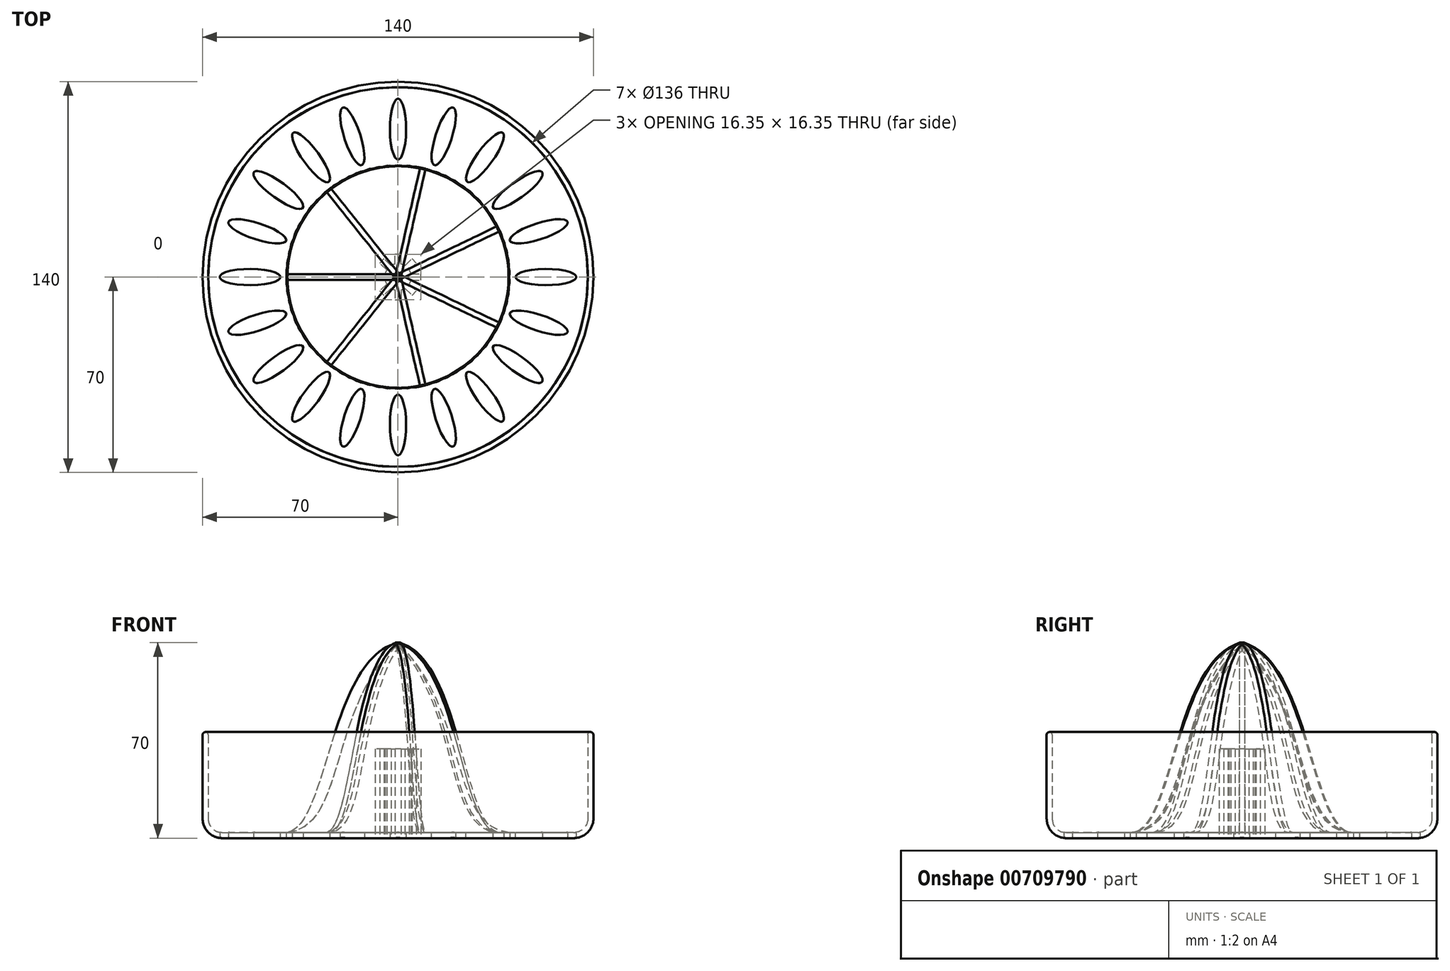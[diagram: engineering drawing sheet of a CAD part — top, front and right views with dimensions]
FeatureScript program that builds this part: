
annotation { "Feature Type Name" : "Feature", "Feature Type Description" : "" }
export const myFeature = defineFeature(function(context is Context, id is Id, definition is map)
    precondition{}
    {
        {
            var Q0;
            Q0=qCreatedBy(makeId("Front.planeOp"),FACE);
            var sketch = newSketch(context, id + "F0", { "sketchPlane" : qUnion([Q0])});
            skFitSpline(sketch, "E0", {"points": [v(0, 68) * mm, v(-40, 0) * mm], "startDerivative": vector(-73.69, -17.1) * mm, "endDerivative": vector(-44.25, -4.31) * mm});
            skLineSegment(sketch, "E1", {"start": v(-63, -2) * mm, "end": v(0, -2) * mm});
            skLineSegment(sketch, "E2", {"start": v(0, -2) * mm, "end": v(0, 68) * mm});
            skLineSegment(sketch, "E3", {"start": v(-70, 5) * mm, "end": v(-70, 35) * mm});
            skLineSegment(sketch, "E4", {"start": v(-69, 36) * mm, "end": v(-69, 36) * mm});
            skLineSegment(sketch, "E5", {"start": v(-68, 35) * mm, "end": v(-68, 5) * mm});
            skLineSegment(sketch, "E6", {"start": v(-63, 0) * mm, "end": v(-40, 0) * mm});
            skPoint(sketch, "E7.visualSharp", {"position": v(-68, 0) * mm});
            skArc(sketch, "E7.filletArc", {"start": v(-68, 5) * mm, "mid": v(-66.54, 1.46) * mm, "end": v(-63, 0) * mm});
            skPoint(sketch, "E8.visualSharp", {"position": v(-70, -2) * mm});
            skArc(sketch, "E8.filletArc", {"start": v(-70, 5) * mm, "mid": v(-67.95, 0.05) * mm, "end": v(-63, -2) * mm});
            skPoint(sketch, "E9.visualSharp", {"position": v(-70, 36) * mm});
            skArc(sketch, "E9.filletArc", {"start": v(-69, 36) * mm, "mid": v(-69.7, 35.7) * mm, "end": v(-70, 35) * mm});
            skPoint(sketch, "E10.visualSharp", {"position": v(-68, 36) * mm});
            skArc(sketch, "E10.filletArc", {"start": v(-68, 35) * mm, "mid": v(-68.3, 35.7) * mm, "end": v(-69, 36) * mm});
            skFitSpline(sketch, "E11", {"points": [v(0, 68) * mm, v(-40, 0) * mm], "startDerivative": vector(-76.4, -73) * mm, "endDerivative": vector(-64.41, -4.31) * mm});
            skLineSegment(sketch, "E12", {"start": v(-40, 0) * mm, "end": v(0, 0) * mm});
            skSolve(sketch);
        }
        {
            var Q0;
            Q0=makeQuery(id+"F0.imprint","IMPRINT",FACE,{"disambiguationData":[TD([[makeQuery(id+"F0.imprint","IMPRINT",EDGE,{"derivedFrom":sQuery(id+"F0.wireOp",EDGE,"E1")}),1.0]])]});
            var Q1;
            {var subQ0=sQuery(id+"F0.wireOp",EDGE,"E11");Q1=makeQuery(id+"F0.imprint","IMPRINT",FACE,{"disambiguationData":[TD([[makeQuery(id+"F0.imprint","IMPRINT",EDGE,{"derivedFrom":subQ0}),1.0]])]});}
            var Q2;
            Q2=sQuery(id+"F0.wireOp",EDGE,"E2");
            revolve(context, id + "F1", {"surfaceOperationType" : NewSurfaceOperationType.NEW, "entities" : qUnion([Q0, Q1]), "axis" : qUnion([Q2]), "revolveType" : RevolveType.FULL});
        }
        {
            var Q0;
            Q0=qCreatedBy(makeId("Top.planeOp"),FACE);
            var sketch = newSketch(context, id + "F2", { "sketchPlane" : qUnion([Q0])});
            skEllipse(sketch, "E13", {"center": v(-52.98, 0) * mm, "majorRadius": 10.85 * mm, "minorRadius": 2.91 * mm, "majorAxis": v(1, 0)});
            skEllipse(sketch, "E14.1.0", {"center": v(-50.4, -16.37) * mm, "majorRadius": 10.85 * mm, "minorRadius": 2.91 * mm, "majorAxis": v(0.95, 0.3)});
            skEllipse(sketch, "E14.2.0", {"center": v(-42.87, -31.14) * mm, "majorRadius": 10.85 * mm, "minorRadius": 2.91 * mm, "majorAxis": v(0.8, 0.59)});
            skEllipse(sketch, "E14.3.0", {"center": v(-31.14, -42.87) * mm, "majorRadius": 10.85 * mm, "minorRadius": 2.91 * mm, "majorAxis": v(0.59, 0.8)});
            skEllipse(sketch, "E14.4.0", {"center": v(-16.37, -50.4) * mm, "majorRadius": 10.85 * mm, "minorRadius": 2.91 * mm, "majorAxis": v(0.3, 0.95)});
            skEllipse(sketch, "E14.5.0", {"center": v(0, -52.98) * mm, "majorRadius": 10.85 * mm, "minorRadius": 2.91 * mm, "majorAxis": v(0, 1)});
            skEllipse(sketch, "E14.6.0", {"center": v(16.37, -50.4) * mm, "majorRadius": 10.85 * mm, "minorRadius": 2.91 * mm, "majorAxis": v(-0.3, 0.95)});
            skEllipse(sketch, "E14.7.0", {"center": v(31.14, -42.87) * mm, "majorRadius": 10.85 * mm, "minorRadius": 2.91 * mm, "majorAxis": v(-0.59, 0.8)});
            skEllipse(sketch, "E14.8.0", {"center": v(42.87, -31.14) * mm, "majorRadius": 10.85 * mm, "minorRadius": 2.91 * mm, "majorAxis": v(-0.8, 0.59)});
            skEllipse(sketch, "E14.9.0", {"center": v(50.4, -16.37) * mm, "majorRadius": 10.85 * mm, "minorRadius": 2.91 * mm, "majorAxis": v(-0.95, 0.3)});
            skEllipse(sketch, "E14.10.0", {"center": v(52.98, 0) * mm, "majorRadius": 10.85 * mm, "minorRadius": 2.91 * mm, "majorAxis": v(-1, 0)});
            skEllipse(sketch, "E14.11.0", {"center": v(50.4, 16.37) * mm, "majorRadius": 10.85 * mm, "minorRadius": 2.91 * mm, "majorAxis": v(-0.95, -0.3)});
            skEllipse(sketch, "E14.12.0", {"center": v(42.87, 31.14) * mm, "majorRadius": 10.85 * mm, "minorRadius": 2.91 * mm, "majorAxis": v(-0.8, -0.59)});
            skEllipse(sketch, "E14.13.0", {"center": v(31.14, 42.87) * mm, "majorRadius": 10.85 * mm, "minorRadius": 2.91 * mm, "majorAxis": v(-0.59, -0.8)});
            skEllipse(sketch, "E14.14.0", {"center": v(16.37, 50.4) * mm, "majorRadius": 10.85 * mm, "minorRadius": 2.91 * mm, "majorAxis": v(-0.3, -0.95)});
            skEllipse(sketch, "E14.15.0", {"center": v(0, 52.98) * mm, "majorRadius": 10.85 * mm, "minorRadius": 2.91 * mm, "majorAxis": v(0, -1)});
            skEllipse(sketch, "E14.16.0", {"center": v(-16.37, 50.4) * mm, "majorRadius": 10.85 * mm, "minorRadius": 2.91 * mm, "majorAxis": v(0.3, -0.95)});
            skEllipse(sketch, "E14.17.0", {"center": v(-31.14, 42.87) * mm, "majorRadius": 10.85 * mm, "minorRadius": 2.91 * mm, "majorAxis": v(0.59, -0.8)});
            skEllipse(sketch, "E14.18.0", {"center": v(-42.87, 31.14) * mm, "majorRadius": 10.85 * mm, "minorRadius": 2.91 * mm, "majorAxis": v(0.8, -0.59)});
            skEllipse(sketch, "E14.19.0", {"center": v(-50.4, 16.37) * mm, "majorRadius": 10.85 * mm, "minorRadius": 2.91 * mm, "majorAxis": v(0.95, -0.3)});
            skPoint(sketch, "E14.center", {"position": v(0, 0) * mm});
            skSolve(sketch);
        }
        {
            var Q0;
            {var subQ0=sQuery(id+"F0.wireOp",EDGE,"E11");Q0=makeQuery(id+"F0.imprint","IMPRINT",FACE,{"disambiguationData":[TD([[makeQuery(id+"F0.imprint","IMPRINT",EDGE,{"derivedFrom":subQ0}),1.0]])]});}
            var Q1;
            Q1=makeQuery(id+"F0.imprint","IMPRINT",FACE,{"disambiguationData":[TD([[makeQuery(id+"F0.imprint","IMPRINT",EDGE,{"derivedFrom":sQuery(id+"F0.wireOp",EDGE,"E0")}),1.0]])]});
            extrude(context, id + "F3", {"entities" : qUnion([Q0, Q1]), "operationType" : NewBodyOperationType.ADD, "endBound" : BoundingType.SYMMETRIC, "depth" : 2 * mm, "offsetDistance" : 25 * mm});
        }
        {
            var Q0;
            Q0=makeQuery(id+"F1.opRevolve","SWEPT_BODY",BODY,{"disambiguationData":[OSD([sQuery(id+"F0.wireOp",EDGE,"E1"),sQuery(id+"F0.wireOp",EDGE,"E2"),sQuery(id+"F0.wireOp",EDGE,"E3"),sQuery(id+"F0.wireOp",EDGE,"E5"),sQuery(id+"F0.wireOp",EDGE,"E6"),sQuery(id+"F0.wireOp",EDGE,"E7.filletArc"),sQuery(id+"F0.wireOp",EDGE,"E8.filletArc"),sQuery(id+"F0.wireOp",EDGE,"E9.filletArc"),sQuery(id+"F0.wireOp",EDGE,"E10.filletArc"),sQuery(id+"F0.wireOp",EDGE,"E11")])]});
            var Q1;
            Q1=sQuery(id+"F0.wireOp",EDGE,"E2");
            circularPattern(context, id + "F4", {"entities" : qUnion([Q0]), "axis" : qUnion([Q1]), "angle" : 360 * degree, "instanceCount" : 7, "equalSpace" : true});
        }
        {
            var Q0;
            Q0=makeQuery(id+"F1.opRevolve","SWEPT_FACE",FACE,{"disambiguationData":[OSD([sQuery(id+"F0.wireOp",EDGE,"E1")])]});
            var sketch = newSketch(context, id + "F5", { "sketchPlane" : qUnion([Q0])});
            skCircle(sketch, "E15", {"center": v(0, 0) * mm, "radius": 4.75 * mm});
            skLineSegment(sketch, "E16.bottom", {"start": v(-1.32, -1.1) * mm, "end": v(-8.18, -1.1) * mm});
            skLineSegment(sketch, "E16.top", {"start": v(-1.32, 1.1) * mm, "end": v(-8.18, 1.1) * mm});
            skLineSegment(sketch, "E16.left", {"start": v(-1.32, -1.1) * mm, "end": v(-1.32, 1.1) * mm});
            skLineSegment(sketch, "E16.right", {"start": v(-8.18, -1.1) * mm, "end": v(-8.18, 1.1) * mm});
            skPoint(sketch, "E16.middle", {"position": v(-4.75, 0) * mm});
            skLineSegment(sketch, "E17.1.0", {"start": v(-1.71, -0.16) * mm, "end": v(-6.56, -5) * mm});
            skLineSegment(sketch, "E17.1.1", {"start": v(-5, -6.56) * mm, "end": v(-6.56, -5) * mm});
            skLineSegment(sketch, "E17.1.2", {"start": v(-0.16, -1.71) * mm, "end": v(-5, -6.56) * mm});
            skLineSegment(sketch, "E17.2.0", {"start": v(-1.1, -1.32) * mm, "end": v(-1.1, -8.18) * mm});
            skLineSegment(sketch, "E17.2.1", {"start": v(1.1, -8.18) * mm, "end": v(-1.1, -8.18) * mm});
            skLineSegment(sketch, "E17.2.2", {"start": v(1.1, -1.32) * mm, "end": v(1.1, -8.18) * mm});
            skLineSegment(sketch, "E18.2.3.0", {"start": v(0.16, -1.71) * mm, "end": v(5, -6.56) * mm});
            skLineSegment(sketch, "E18.3.3.0", {"start": v(6.56, -5) * mm, "end": v(5, -6.56) * mm});
            skLineSegment(sketch, "E18.6.3.0", {"start": v(1.71, -0.16) * mm, "end": v(6.56, -5) * mm});
            skLineSegment(sketch, "E18.2.4.0", {"start": v(1.32, -1.1) * mm, "end": v(8.18, -1.1) * mm});
            skLineSegment(sketch, "E18.3.4.0", {"start": v(8.18, 1.1) * mm, "end": v(8.18, -1.1) * mm});
            skLineSegment(sketch, "E18.6.4.0", {"start": v(1.32, 1.1) * mm, "end": v(8.18, 1.1) * mm});
            skLineSegment(sketch, "E18.2.5.0", {"start": v(1.71, 0.16) * mm, "end": v(6.56, 5) * mm});
            skLineSegment(sketch, "E18.3.5.0", {"start": v(5, 6.56) * mm, "end": v(6.56, 5) * mm});
            skLineSegment(sketch, "E18.6.5.0", {"start": v(0.16, 1.71) * mm, "end": v(5, 6.56) * mm});
            skLineSegment(sketch, "E18.2.6.0", {"start": v(1.1, 1.32) * mm, "end": v(1.1, 8.18) * mm});
            skLineSegment(sketch, "E18.3.6.0", {"start": v(-1.1, 8.18) * mm, "end": v(1.1, 8.18) * mm});
            skLineSegment(sketch, "E18.6.6.0", {"start": v(-1.1, 1.32) * mm, "end": v(-1.1, 8.18) * mm});
            skLineSegment(sketch, "E18.2.7.0", {"start": v(-0.16, 1.71) * mm, "end": v(-5, 6.56) * mm});
            skLineSegment(sketch, "E18.3.7.0", {"start": v(-6.56, 5) * mm, "end": v(-5, 6.56) * mm});
            skLineSegment(sketch, "E18.6.7.0", {"start": v(-1.71, 0.16) * mm, "end": v(-6.56, 5) * mm});
            skSolve(sketch);
        }
        {
            var Q0;
            Q0 = qSketchRegion(id + "F2", true);
            extrude(context, id + "F6", {"entities" : qUnion([Q0]), "operationType" : NewBodyOperationType.REMOVE, "endBound" : BoundingType.SYMMETRIC, "oppositeDirection" : true, "depth" : 25 * mm, "offsetDistance" : 25 * mm});
        }
        {
            var Q0;
            {var subQ5=sQuery(id+"F5.wireOp",EDGE,"E18.3.7.0");Q0=makeQuery(id+"F5.imprint","IMPRINT",FACE,{"disambiguationData":[TD([[makeQuery(id+"F5.imprint","IMPRINT",EDGE,{"derivedFrom":subQ5}),-1.0]])]});}
            var Q1;
            {var subQ5=sQuery(id+"F5.wireOp",EDGE,"E18.3.6.0");Q1=makeQuery(id+"F5.imprint","IMPRINT",FACE,{"disambiguationData":[TD([[makeQuery(id+"F5.imprint","IMPRINT",EDGE,{"derivedFrom":subQ5}),-1.0]])]});}
            var Q2;
            {var subQ5=sQuery(id+"F5.wireOp",EDGE,"E18.3.5.0");Q2=makeQuery(id+"F5.imprint","IMPRINT",FACE,{"disambiguationData":[TD([[makeQuery(id+"F5.imprint","IMPRINT",EDGE,{"derivedFrom":subQ5}),-1.0]])]});}
            var Q3;
            {var subQ28=sQuery(id+"F5.wireOp",EDGE,"E16.left");Q3=makeQuery(id+"F5.imprint","IMPRINT",FACE,{"disambiguationData":[TD([[makeQuery(id+"F5.imprint","IMPRINT",EDGE,{"derivedFrom":subQ28}),-1.0]])]});}
            var Q4;
            {var subQ0=sQuery(id+"F5.wireOp",EDGE,"E16.left");Q4=makeQuery(id+"F5.imprint","IMPRINT",FACE,{"disambiguationData":[TD([[makeQuery(id+"F5.imprint","IMPRINT",EDGE,{"derivedFrom":subQ0}),1.0]])]});}
            var Q5;
            {var subQ5=sQuery(id+"F5.wireOp",EDGE,"E16.right");Q5=makeQuery(id+"F5.imprint","IMPRINT",FACE,{"disambiguationData":[TD([[makeQuery(id+"F5.imprint","IMPRINT",EDGE,{"derivedFrom":subQ5}),-1.0]])]});}
            var Q6;
            {var subQ5=sQuery(id+"F5.wireOp",EDGE,"E17.1.1");Q6=makeQuery(id+"F5.imprint","IMPRINT",FACE,{"disambiguationData":[TD([[makeQuery(id+"F5.imprint","IMPRINT",EDGE,{"derivedFrom":subQ5}),-1.0]])]});}
            var Q7;
            {var subQ5=sQuery(id+"F5.wireOp",EDGE,"E17.2.1");Q7=makeQuery(id+"F5.imprint","IMPRINT",FACE,{"disambiguationData":[TD([[makeQuery(id+"F5.imprint","IMPRINT",EDGE,{"derivedFrom":subQ5}),-1.0]])]});}
            var Q8;
            {var subQ5=sQuery(id+"F5.wireOp",EDGE,"E18.3.3.0");Q8=makeQuery(id+"F5.imprint","IMPRINT",FACE,{"disambiguationData":[TD([[makeQuery(id+"F5.imprint","IMPRINT",EDGE,{"derivedFrom":subQ5}),-1.0]])]});}
            var Q9;
            {var subQ5=sQuery(id+"F5.wireOp",EDGE,"E18.3.4.0");Q9=makeQuery(id+"F5.imprint","IMPRINT",FACE,{"disambiguationData":[TD([[makeQuery(id+"F5.imprint","IMPRINT",EDGE,{"derivedFrom":subQ5}),-1.0]])]});}
            var Q10;
            {var subQ0=sQuery(id+"F5.wireOp",EDGE,"E18.2.5.0");var subQ1=sQuery(id+"F5.wireOp",EDGE,"E15");var subQ2=makeQuery(id+"F5.imprint","INTERSECT",VERTEX,{"derivedFrom":[subQ1,subQ0]});Q10=makeQuery(id+"F5.imprint","IMPRINT",FACE,{"disambiguationData":[TD([[makeQuery(id+"F5.imprint","IMPRINT",EDGE,{"disambiguationData":[TD([[subQ2,1.0]])],"derivedFrom":subQ1}),1.0]])]});}
            var Q11;
            {var subQ0=sQuery(id+"F5.wireOp",EDGE,"E18.6.6.0");var subQ1=sQuery(id+"F5.wireOp",EDGE,"E15");var subQ2=makeQuery(id+"F5.imprint","INTERSECT",VERTEX,{"derivedFrom":[subQ1,subQ0]});Q11=makeQuery(id+"F5.imprint","IMPRINT",FACE,{"disambiguationData":[TD([[makeQuery(id+"F5.imprint","IMPRINT",EDGE,{"disambiguationData":[TD([[subQ2,-1.0]])],"derivedFrom":subQ1}),1.0]])]});}
            var Q12;
            {var subQ0=sQuery(id+"F5.wireOp",EDGE,"E18.6.7.0");var subQ1=sQuery(id+"F5.wireOp",EDGE,"E15");var subQ2=makeQuery(id+"F5.imprint","INTERSECT",VERTEX,{"derivedFrom":[subQ1,subQ0]});Q12=makeQuery(id+"F5.imprint","IMPRINT",FACE,{"disambiguationData":[TD([[makeQuery(id+"F5.imprint","IMPRINT",EDGE,{"disambiguationData":[TD([[subQ2,-1.0]])],"derivedFrom":subQ1}),1.0]])]});}
            var Q13;
            {var subQ0=sQuery(id+"F5.wireOp",EDGE,"E16.bottom");var subQ1=sQuery(id+"F5.wireOp",EDGE,"E15");var subQ2=makeQuery(id+"F5.imprint","INTERSECT",VERTEX,{"derivedFrom":[subQ1,subQ0]});Q13=makeQuery(id+"F5.imprint","IMPRINT",FACE,{"disambiguationData":[TD([[makeQuery(id+"F5.imprint","IMPRINT",EDGE,{"disambiguationData":[TD([[subQ2,-1.0]])],"derivedFrom":subQ1}),1.0]])]});}
            var Q14;
            {var subQ0=sQuery(id+"F5.wireOp",EDGE,"E17.1.2");var subQ1=sQuery(id+"F5.wireOp",EDGE,"E15");var subQ2=makeQuery(id+"F5.imprint","INTERSECT",VERTEX,{"derivedFrom":[subQ1,subQ0]});Q14=makeQuery(id+"F5.imprint","IMPRINT",FACE,{"disambiguationData":[TD([[makeQuery(id+"F5.imprint","IMPRINT",EDGE,{"disambiguationData":[TD([[subQ2,-1.0]])],"derivedFrom":subQ1}),1.0]])]});}
            var Q15;
            {var subQ0=sQuery(id+"F5.wireOp",EDGE,"E17.2.2");var subQ1=sQuery(id+"F5.wireOp",EDGE,"E15");var subQ2=makeQuery(id+"F5.imprint","INTERSECT",VERTEX,{"derivedFrom":[subQ1,subQ0]});Q15=makeQuery(id+"F5.imprint","IMPRINT",FACE,{"disambiguationData":[TD([[makeQuery(id+"F5.imprint","IMPRINT",EDGE,{"disambiguationData":[TD([[subQ2,-1.0]])],"derivedFrom":subQ1}),1.0]])]});}
            var Q16;
            {var subQ0=sQuery(id+"F5.wireOp",EDGE,"E18.6.3.0");var subQ1=sQuery(id+"F5.wireOp",EDGE,"E15");var subQ2=makeQuery(id+"F5.imprint","INTERSECT",VERTEX,{"derivedFrom":[subQ1,subQ0]});Q16=makeQuery(id+"F5.imprint","IMPRINT",FACE,{"disambiguationData":[TD([[makeQuery(id+"F5.imprint","IMPRINT",EDGE,{"disambiguationData":[TD([[subQ2,-1.0]])],"derivedFrom":subQ1}),1.0]])]});}
            var Q17;
            {var subQ0=sQuery(id+"F5.wireOp",EDGE,"E18.6.5.0");var subQ1=sQuery(id+"F5.wireOp",EDGE,"E15");var subQ2=makeQuery(id+"F5.imprint","INTERSECT",VERTEX,{"derivedFrom":[subQ1,subQ0]});Q17=makeQuery(id+"F5.imprint","IMPRINT",FACE,{"disambiguationData":[TD([[makeQuery(id+"F5.imprint","IMPRINT",EDGE,{"disambiguationData":[TD([[subQ2,-1.0]])],"derivedFrom":subQ1}),1.0]])]});}
            extrude(context, id + "F7", {"entities" : qUnion([Q0, Q1, Q2, Q3, Q4, Q5, Q6, Q7, Q8, Q9, Q10, Q11, Q12, Q13, Q14, Q15, Q16, Q17]), "operationType" : NewBodyOperationType.REMOVE, "oppositeDirection" : true, "depth" : 32 * mm, "offsetDistance" : 25 * mm});
        }
    });
